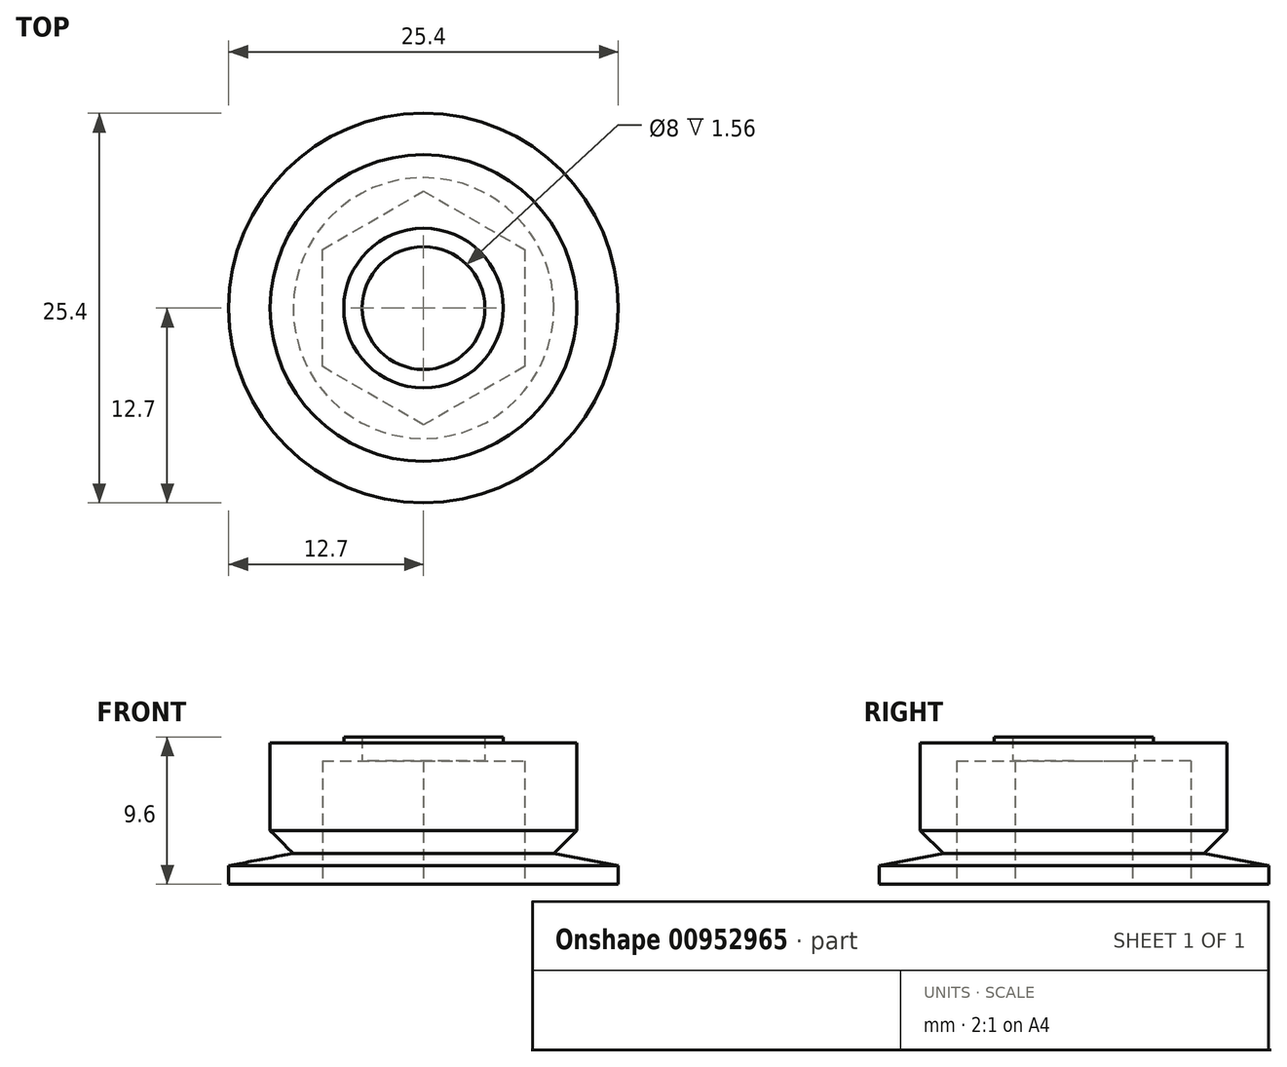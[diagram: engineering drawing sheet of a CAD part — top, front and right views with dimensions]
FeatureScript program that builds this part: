
annotation { "Feature Type Name" : "Feature", "Feature Type Description" : "" }
export const myFeature = defineFeature(function(context is Context, id is Id, definition is map)
    precondition{}
    {
        {
            var Q0;
            Q0=qCreatedBy(makeId("Front.planeOp"),FACE);
            var sketch = newSketch(context, id + "F0", { "sketchPlane" : qUnion([Q0])});
            skLineSegment(sketch, "E0", {"start": v(4, 0) * mm, "end": v(12.7, 0) * mm});
            skLineSegment(sketch, "E1", {"start": v(12.7, 0) * mm, "end": v(12.7, 1.2) * mm});
            skLineSegment(sketch, "E2", {"start": v(12.7, 1.2) * mm, "end": v(8.5, 2) * mm});
            skLineSegment(sketch, "E3", {"start": v(10, 3.5) * mm, "end": v(10, 9.2) * mm});
            skLineSegment(sketch, "E4", {"start": v(10, 9.2) * mm, "end": v(5.2, 9.2) * mm});
            skLineSegment(sketch, "E5", {"start": v(4, 9.6) * mm, "end": v(4, 0) * mm});
            skLineSegment(sketch, "E6", {"start": v(8.5, 2) * mm, "end": v(10, 3.5) * mm});
            skLineSegment(sketch, "E7", {"start": v(5.2, 9.2) * mm, "end": v(5.2, 9.6) * mm});
            skLineSegment(sketch, "E8", {"start": v(5.2, 9.6) * mm, "end": v(4, 9.6) * mm});
            skSolve(sketch);
        }
        {
            var Q0;
            Q0=qCreatedBy(makeId("Top.planeOp"),FACE);
            var sketch = newSketch(context, id + "F1", { "sketchPlane" : qUnion([Q0])});
            skCircle(sketch, "E9", {"center": v(0, 0) * mm, "radius": 1.74 * mm});
            skSolve(sketch);
        }
        {
            var Q0;
            Q0=sQuery(id+"F1.wireOp",EDGE,"E9");
            extrude(context, id + "F2", {"bodyType" : ToolBodyType.SURFACE, "surfaceEntities" : qUnion([Q0]), "depth" : 25 * mm, "offsetDistance" : 25 * mm});
        }
        {
            var Q0;
            Q0=makeQuery(id+"F0.imprint","IMPRINT",FACE,{"disambiguationData":[TD([[makeQuery(id+"F0.imprint","IMPRINT",EDGE,{"derivedFrom":sQuery(id+"F0.wireOp",EDGE,"E0")}),1.0]])]});
            var Q1;
            Q1=makeQuery(id+"F2.opExtrude","SWEPT_FACE",FACE,{"disambiguationData":[OSD([sQuery(id+"F1.wireOp",EDGE,"E9")])]});
            revolve(context, id + "F3", {"surfaceOperationType" : NewSurfaceOperationType.NEW, "entities" : qUnion([Q0]), "axis" : qUnion([Q1]), "revolveType" : RevolveType.FULL});
        }
        {
            var Q0;
            Q0=qCreatedBy(makeId("Top.planeOp"),FACE);
            var sketch = newSketch(context, id + "F4", { "sketchPlane" : qUnion([Q0])});
            skCircle(sketch, "E10.cCircle", {"center": v(0, 0) * mm, "radius": 6.6 * mm, "construction": true});
            skLineSegment(sketch, "E10.0", {"start": v(0, 7.62) * mm, "end": v(6.6, 3.81) * mm});
            skLineSegment(sketch, "E10.1", {"start": v(6.6, 3.81) * mm, "end": v(6.6, -3.81) * mm});
            skLineSegment(sketch, "E10.2", {"start": v(6.6, -3.81) * mm, "end": v(0, -7.62) * mm});
            skLineSegment(sketch, "E10.3", {"start": v(0, -7.62) * mm, "end": v(-6.6, -3.81) * mm});
            skLineSegment(sketch, "E10.4", {"start": v(-6.6, -3.81) * mm, "end": v(-6.6, 3.81) * mm});
            skLineSegment(sketch, "E10.5", {"start": v(-6.6, 3.81) * mm, "end": v(0, 7.62) * mm});
            skPoint(sketch, "E10.0.midPoint", {"position": v(3.3, 5.72) * mm});
            skSolve(sketch);
        }
        {
            var Q0;
            Q0 = qSketchRegion(id + "F4", true);
            extrude(context, id + "F5", {"entities" : qUnion([Q0]), "operationType" : NewBodyOperationType.REMOVE, "oppositeDirection" : true, "depth" : 0 * mm, "offsetDistance" : 25 * mm, "hasSecondDirection" : true, "secondDirectionOppositeDirection" : false, "secondDirectionDepth" : 8.04 * mm});
        }
    });
